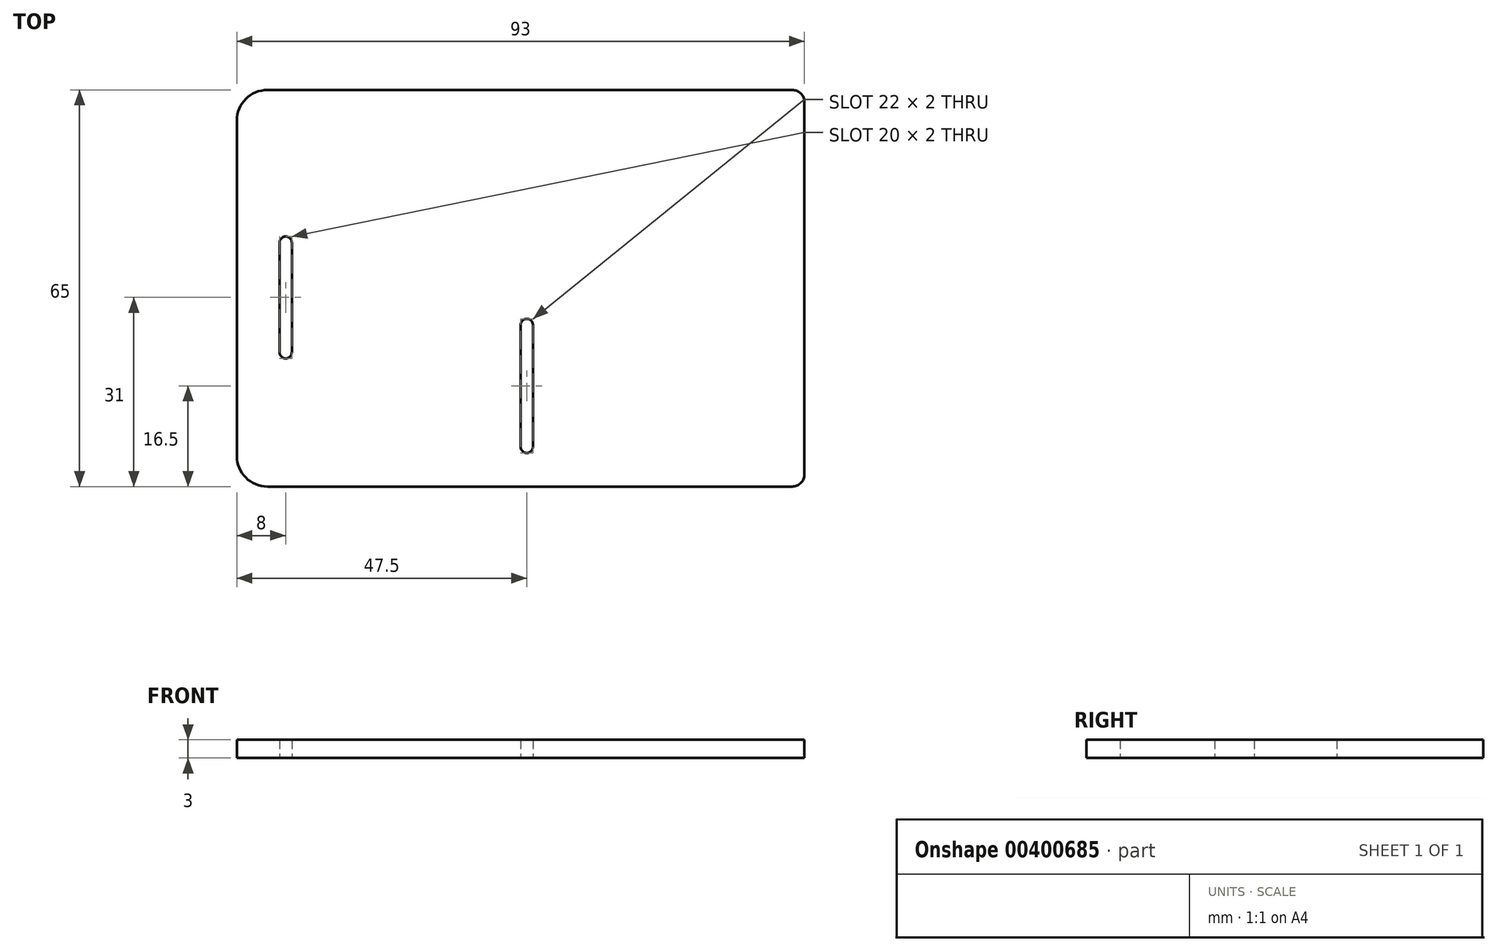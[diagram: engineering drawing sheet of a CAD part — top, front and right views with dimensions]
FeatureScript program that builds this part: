
annotation { "Feature Type Name" : "Feature", "Feature Type Description" : "" }
export const myFeature = defineFeature(function(context is Context, id is Id, definition is map)
    precondition{}
    {
        {
            var Q0;
            Q0=qCreatedBy(makeId("Top.planeOp"),FACE);
            var sketch = newSketch(context, id + "F0", { "sketchPlane" : qUnion([Q0])});
            skLineSegment(sketch, "E0.bottom", {"start": v(46.5, -32.5) * mm, "end": v(-46.5, -32.5) * mm});
            skLineSegment(sketch, "E0.top", {"start": v(46.5, 32.5) * mm, "end": v(-46.5, 32.5) * mm});
            skLineSegment(sketch, "E0.left", {"start": v(46.5, -32.5) * mm, "end": v(46.5, 32.5) * mm});
            skLineSegment(sketch, "E0.right", {"start": v(-46.5, -32.5) * mm, "end": v(-46.5, 32.5) * mm});
            skPoint(sketch, "E0.middle", {"position": v(0, 0) * mm});
            skLineSegment(sketch, "E1", {"start": v(-39.5, 7.5) * mm, "end": v(-39.5, -10.5) * mm});
            skLineSegment(sketch, "E2.0", {"start": v(-37.5, 7.5) * mm, "end": v(-37.5, -10.5) * mm});
            skArc(sketch, "E3", {"start": v(-37.5, 7.5) * mm, "mid": v(-38.5, 8.5) * mm, "end": v(-39.5, 7.5) * mm});
            skArc(sketch, "E4", {"start": v(-39.5, -10.5) * mm, "mid": v(-38.5, -11.5) * mm, "end": v(-37.5, -10.5) * mm});
            skLineSegment(sketch, "E5", {"start": v(2, -26) * mm, "end": v(2, -6) * mm});
            skLineSegment(sketch, "E6.0", {"start": v(0, -26) * mm, "end": v(0, -6) * mm});
            skArc(sketch, "E7", {"start": v(2, -6) * mm, "mid": v(1, -5) * mm, "end": v(0, -6) * mm});
            skArc(sketch, "E8", {"start": v(0, -26) * mm, "mid": v(1, -27) * mm, "end": v(2, -26) * mm});
            skSolve(sketch);
        }
        {
            var Q0;
            Q0=makeQuery(id+"F0.imprint","IMPRINT",FACE,{"disambiguationData":[TD([[makeQuery(id+"F0.imprint","IMPRINT",EDGE,{"derivedFrom":sQuery(id+"F0.wireOp",EDGE,"E0.bottom")}),-1.0]])]});
            extrude(context, id + "F1", {"entities" : qUnion([Q0]), "depth" : 3 * mm});
        }
        {
            var Q0;
            Q0=makeQuery(id+"F1.opExtrude","SWEPT_EDGE",EDGE,{"disambiguationData":[OSD([sQuery(id+"F0.wireOp",EDGE,"E0.top"),sQuery(id+"F0.wireOp",EDGE,"E0.right")])]});
            var Q1;
            Q1=makeQuery(id+"F1.opExtrude","SWEPT_EDGE",EDGE,{"disambiguationData":[OSD([sQuery(id+"F0.wireOp",EDGE,"E0.bottom"),sQuery(id+"F0.wireOp",EDGE,"E0.right")])]});
            fillet(context, id + "F2", {"entities" : qUnion([Q0, Q1]), "radius" : 5 * mm, "tangentPropagation" : true, "allowEdgeOverflow" : false});
        }
        {
            var Q0;
            Q0=makeQuery(id+"F1.opExtrude","SWEPT_EDGE",EDGE,{"disambiguationData":[OSD([sQuery(id+"F0.wireOp",EDGE,"E0.bottom"),sQuery(id+"F0.wireOp",EDGE,"E0.left")])]});
            var Q1;
            Q1=makeQuery(id+"F1.opExtrude","SWEPT_EDGE",EDGE,{"disambiguationData":[OSD([sQuery(id+"F0.wireOp",EDGE,"E0.top"),sQuery(id+"F0.wireOp",EDGE,"E0.left")])]});
            fillet(context, id + "F3", {"entities" : qUnion([Q0, Q1]), "radius" : 2 * mm, "tangentPropagation" : true, "allowEdgeOverflow" : false});
        }
    });
